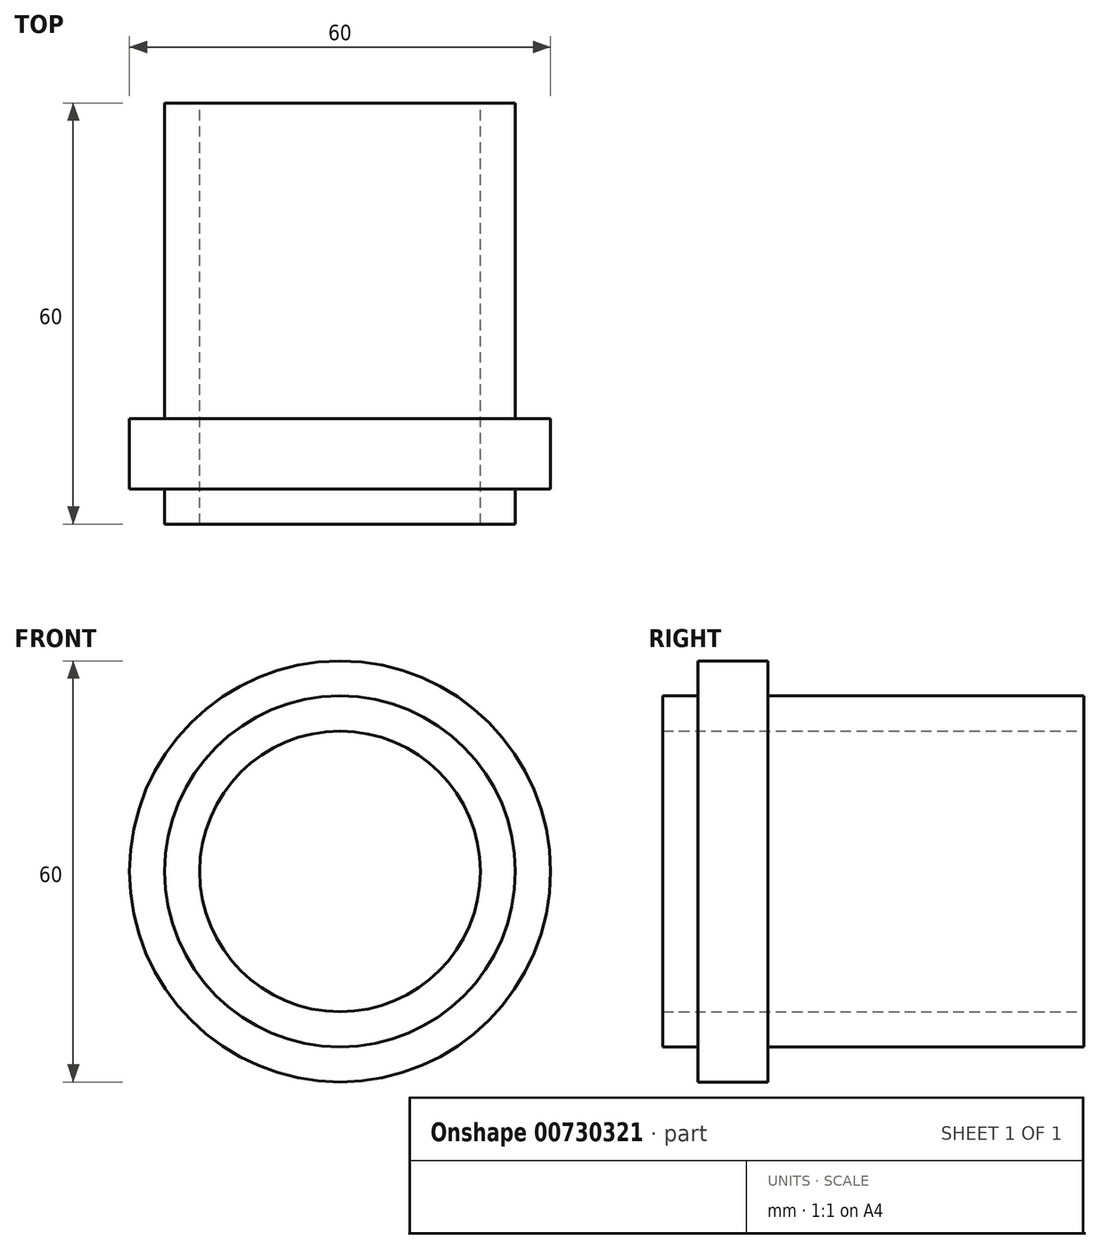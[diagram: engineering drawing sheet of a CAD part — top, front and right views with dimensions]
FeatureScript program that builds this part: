
annotation { "Feature Type Name" : "Feature", "Feature Type Description" : "" }
export const myFeature = defineFeature(function(context is Context, id is Id, definition is map)
    precondition{}
    {
        {
            var Q0;
            Q0=qCreatedBy(makeId("Front.planeOp"),FACE);
            var sketch = newSketch(context, id + "F0", { "sketchPlane" : qUnion([Q0])});
            skCircle(sketch, "E0", {"center": v(0, 0) * mm, "radius": 25 * mm});
            skCircle(sketch, "E1", {"center": v(0, 0) * mm, "radius": 20 * mm});
            skSolve(sketch);
        }
        {
            var Q0;
            Q0 = qSketchRegion(id + "F0", true);
            extrude(context, id + "F1", {"entities" : qUnion([Q0]), "depth" : 10 * mm, "offsetDistance" : 25 * mm, "hasSecondDirection" : true, "secondDirectionOppositeDirection" : true, "secondDirectionDepth" : 50 * mm});
        }
        {
            var Q0;
            Q0=qCreatedBy(makeId("Front.planeOp"),FACE);
            var sketch = newSketch(context, id + "F2", { "sketchPlane" : qUnion([Q0])});
            skCircle(sketch, "E2", {"center": v(0, 0) * mm, "radius": 30 * mm});
            skCircle(sketch, "E3", {"center": v(0, 0) * mm, "radius": 25 * mm});
            skSolve(sketch);
        }
        {
            var Q0;
            Q0 = qSketchRegion(id + "F2", true);
            extrude(context, id + "F3", {"entities" : qUnion([Q0]), "operationType" : NewBodyOperationType.ADD, "oppositeDirection" : true, "depth" : 10 * mm, "offsetDistance" : 25 * mm, "symmetric" : true});
        }
    });
